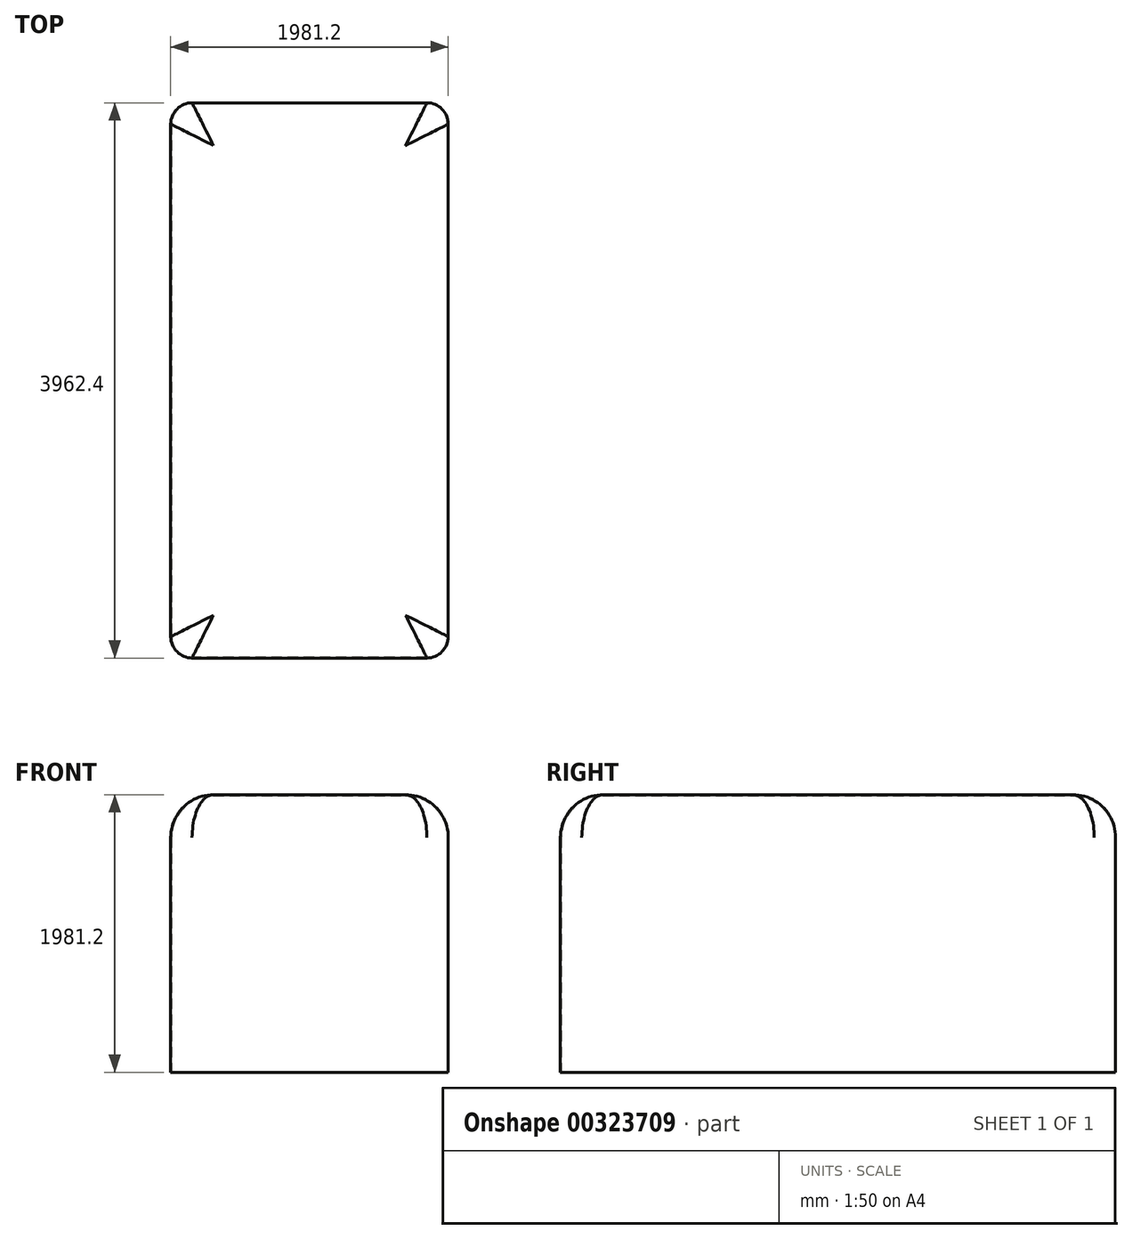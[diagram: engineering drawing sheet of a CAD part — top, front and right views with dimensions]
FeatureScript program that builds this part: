
annotation { "Feature Type Name" : "Feature", "Feature Type Description" : "" }
export const myFeature = defineFeature(function(context is Context, id is Id, definition is map)
    precondition{}
    {
        {
            var Q0;
            Q0=qCreatedBy(makeId("Top.planeOp"),FACE);
            var sketch = newSketch(context, id + "F0", { "sketchPlane" : qUnion([Q0])});
            skLineSegment(sketch, "E0.bottom", {"start": v(990.6, 1981.2) * mm, "end": v(-990.6, 1981.2) * mm});
            skLineSegment(sketch, "E0.top", {"start": v(990.6, -1981.2) * mm, "end": v(-990.6, -1981.2) * mm});
            skLineSegment(sketch, "E0.left", {"start": v(990.6, 1981.2) * mm, "end": v(990.6, -1981.2) * mm});
            skLineSegment(sketch, "E0.right", {"start": v(-990.6, 1981.2) * mm, "end": v(-990.6, -1981.2) * mm});
            skPoint(sketch, "E0.middle", {"position": v(0, 0) * mm});
            skSolve(sketch);
        }
        {
            var Q0;
            Q0 = qSketchRegion(id + "F0", true);
            extrude(context, id + "F1", {"entities" : qUnion([Q0]), "depth" : 1981.2 * mm});
        }
        {
            var Q0;
            Q0=makeQuery(id+"F1.opExtrude","SWEPT_EDGE",EDGE,{"disambiguationData":[OSD([sQuery(id+"F0.wireOp",EDGE,"E0.top"),sQuery(id+"F0.wireOp",EDGE,"E0.right")])]});
            var Q1;
            Q1=makeQuery(id+"F1.opExtrude","SWEPT_EDGE",EDGE,{"disambiguationData":[OSD([sQuery(id+"F0.wireOp",EDGE,"E0.bottom"),sQuery(id+"F0.wireOp",EDGE,"E0.left")])]});
            var Q2;
            Q2=makeQuery(id+"F1.opExtrude","SWEPT_EDGE",EDGE,{"disambiguationData":[OSD([sQuery(id+"F0.wireOp",EDGE,"E0.top"),sQuery(id+"F0.wireOp",EDGE,"E0.left")])]});
            var Q3;
            Q3=makeQuery(id+"F1.opExtrude","SWEPT_EDGE",EDGE,{"disambiguationData":[OSD([sQuery(id+"F0.wireOp",EDGE,"E0.bottom"),sQuery(id+"F0.wireOp",EDGE,"E0.right")])]});
            fillet(context, id + "F2", {"entities" : qUnion([Q0, Q1, Q2, Q3]), "radius" : 152.4 * mm, "tangentPropagation" : true, "allowEdgeOverflow" : false});
        }
        {
            var Q0;
            Q0=makeQuery(id+"F1.opExtrude","CAP_EDGE",EDGE,{"disambiguationData":[OSD([sQuery(id+"F0.wireOp",EDGE,"E0.left")])],"isStart":false});
            var Q1;
            Q1=makeQuery(id+"F1.opExtrude","CAP_EDGE",EDGE,{"disambiguationData":[OSD([sQuery(id+"F0.wireOp",EDGE,"E0.top")])],"isStart":false});
            var Q2;
            Q2=makeQuery(id+"F1.opExtrude","CAP_EDGE",EDGE,{"disambiguationData":[OSD([sQuery(id+"F0.wireOp",EDGE,"E0.right")])],"isStart":false});
            var Q3;
            Q3=makeQuery(id+"F1.opExtrude","CAP_EDGE",EDGE,{"disambiguationData":[OSD([sQuery(id+"F0.wireOp",EDGE,"E0.bottom")])],"isStart":false});
            fillet(context, id + "F3", {"entities" : qUnion([Q0, Q1, Q2, Q3]), "radius" : 304.8 * mm, "tangentPropagation" : true, "allowEdgeOverflow" : false});
        }
        {
            var Q0;
            Q0=makeQuery(id+"F1.opExtrude","CAP_FACE",FACE,{"disambiguationData":[OSD([sQuery(id+"F0.wireOp",EDGE,"E0.bottom"),sQuery(id+"F0.wireOp",EDGE,"E0.top"),sQuery(id+"F0.wireOp",EDGE,"E0.left"),sQuery(id+"F0.wireOp",EDGE,"E0.right")])],"isStart":true});
            shell(context, id + "F4", {"entities" : qUnion([Q0]), "thickness" : 6.35 * mm});
        }
        {
            var Q0;
            Q0=makeQuery(id+"F1.opExtrude","CAP_FACE",FACE,{"disambiguationData":[OSD([sQuery(id+"F0.wireOp",EDGE,"E0.bottom"),sQuery(id+"F0.wireOp",EDGE,"E0.top"),sQuery(id+"F0.wireOp",EDGE,"E0.left"),sQuery(id+"F0.wireOp",EDGE,"E0.right")])],"isStart":true});
            var Q1;
            Q1=makeQuery(id+"F1.opExtrude","SWEPT_BODY",BODY,{"disambiguationData":[OSD([sQuery(id+"F0.wireOp",EDGE,"E0.bottom"),sQuery(id+"F0.wireOp",EDGE,"E0.top"),sQuery(id+"F0.wireOp",EDGE,"E0.left"),sQuery(id+"F0.wireOp",EDGE,"E0.right")])]});
            shell(context, id + "F5", {"isHollow" : true, "entities" : qUnion([Q0]), "parts" : qUnion([Q1]), "thickness" : 2.54 * mm});
        }
    });
